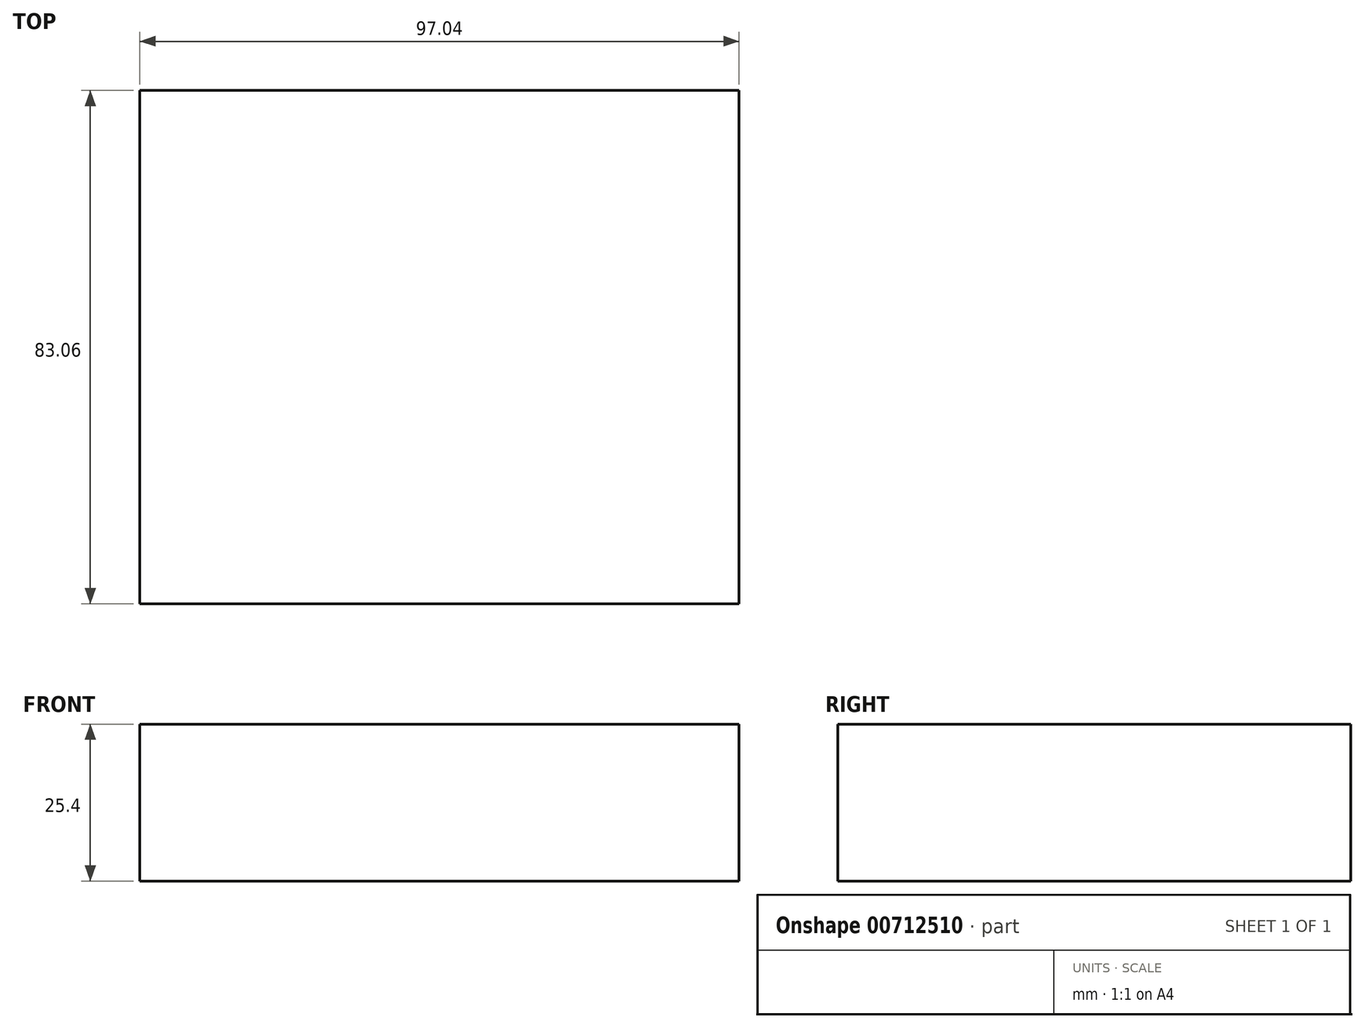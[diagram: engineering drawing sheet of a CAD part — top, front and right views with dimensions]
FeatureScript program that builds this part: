
annotation { "Feature Type Name" : "Feature", "Feature Type Description" : "" }
export const myFeature = defineFeature(function(context is Context, id is Id, definition is map)
    precondition{}
    {
        {
            var Q0;
            Q0=qCreatedBy(makeId("Top.planeOp"),FACE);
            var sketch = newSketch(context, id + "F0", { "sketchPlane" : qUnion([Q0])});
            skLineSegment(sketch, "E0.bottom", {"start": v(-48.52, -41.53) * mm, "end": v(48.52, -41.53) * mm});
            skLineSegment(sketch, "E0.top", {"start": v(-48.52, 41.53) * mm, "end": v(48.52, 41.53) * mm});
            skLineSegment(sketch, "E0.left", {"start": v(-48.52, -41.53) * mm, "end": v(-48.52, 41.53) * mm});
            skLineSegment(sketch, "E0.right", {"start": v(48.52, -41.53) * mm, "end": v(48.52, 41.53) * mm});
            skPoint(sketch, "E0.middle", {"position": v(0, 0) * mm});
            skSolve(sketch);
        }
        {
            var Q0;
            Q0=makeQuery(id+"F0.imprint","IMPRINT",FACE,{"disambiguationData":[TD([[makeQuery(id+"F0.imprint","IMPRINT",EDGE,{"derivedFrom":sQuery(id+"F0.wireOp",EDGE,"E0.bottom")}),1.0]])]});
            extrude(context, id + "F1", {"entities" : qUnion([Q0]), "depth" : 25.4 * mm, "offsetDistance" : 25.4 * mm});
        }
    });
